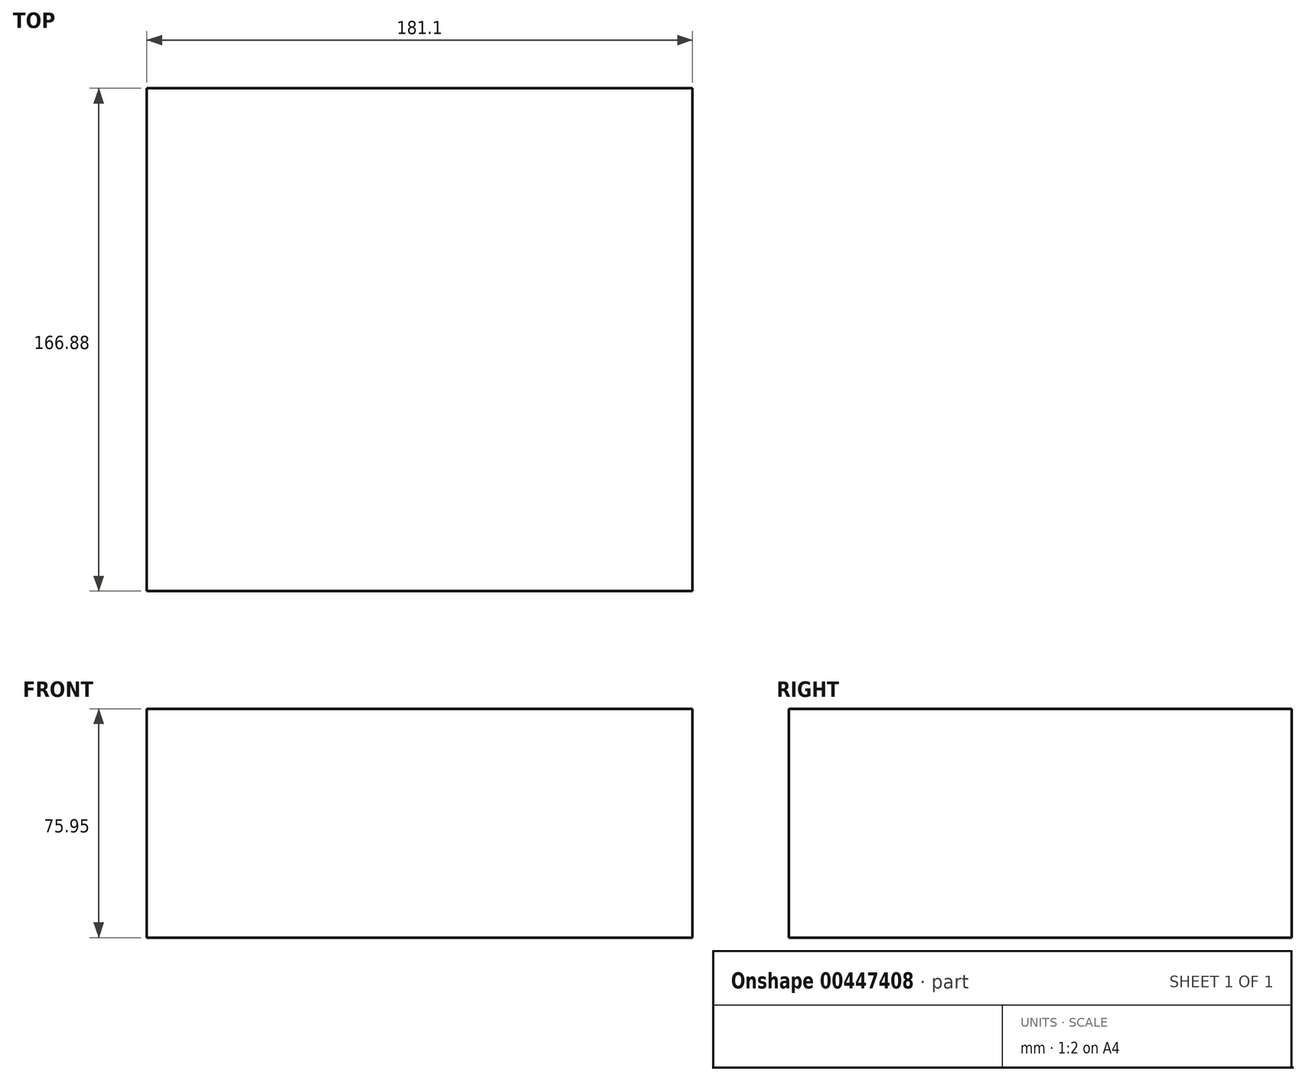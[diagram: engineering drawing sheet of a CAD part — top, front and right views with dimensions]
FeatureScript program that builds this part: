
annotation { "Feature Type Name" : "Feature", "Feature Type Description" : "" }
export const myFeature = defineFeature(function(context is Context, id is Id, definition is map)
    precondition{}
    {
        {
            var Q0;
            Q0=qCreatedBy(makeId("Front.planeOp"),FACE);
            var sketch = newSketch(context, id + "F0", { "sketchPlane" : qUnion([Q0])});
            skLineSegment(sketch, "E0.bottom", {"start": v(0, 0) * mm, "end": v(-181.1, 0) * mm});
            skLineSegment(sketch, "E0.top", {"start": v(0, 75.95) * mm, "end": v(-181.1, 75.95) * mm});
            skLineSegment(sketch, "E0.left", {"start": v(0, 0) * mm, "end": v(0, 75.95) * mm});
            skLineSegment(sketch, "E0.right", {"start": v(-181.1, 0) * mm, "end": v(-181.1, 75.95) * mm});
            skSolve(sketch);
        }
        {
            var Q0;
            Q0 = qSketchRegion(id + "F0", true);
            extrude(context, id + "F1", {"entities" : qUnion([Q0]), "depth" : 166.88 * mm});
        }
    });
